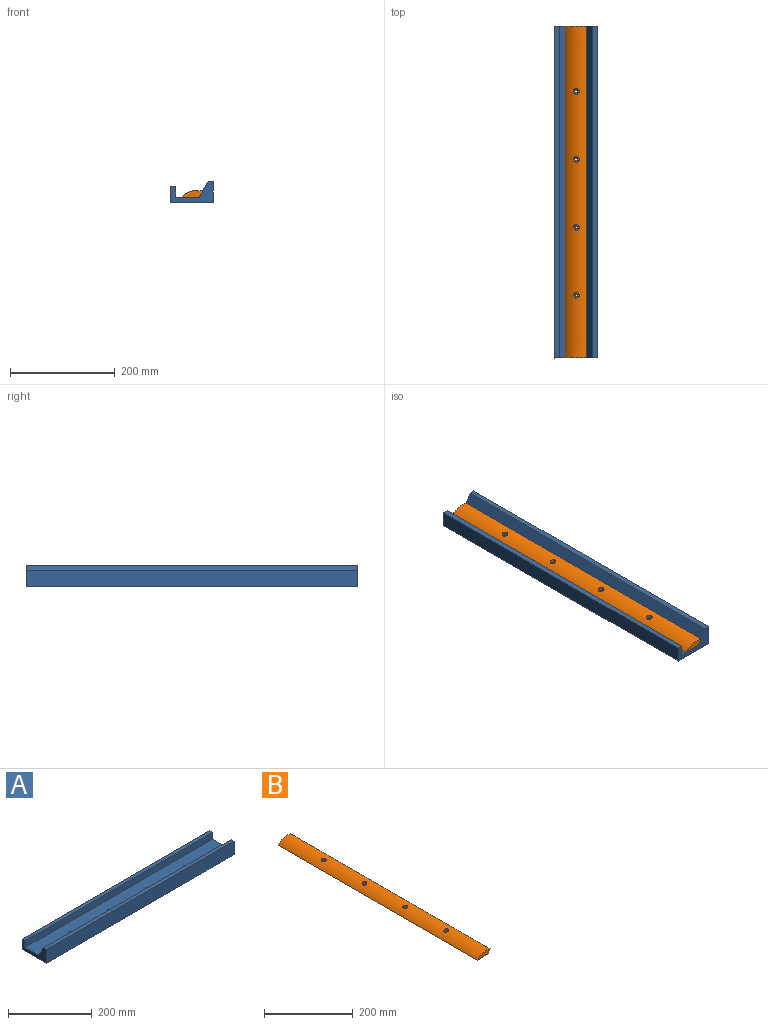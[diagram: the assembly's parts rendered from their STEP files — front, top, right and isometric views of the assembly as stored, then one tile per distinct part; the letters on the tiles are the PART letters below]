
ASSEMBLY  parts=2 mates=1
PART A: 14 faces, bbox 635x82x40 mm
  f0: plane 635x10mm, normal (0,0,1), area 6350mm2, adj f1,f2,f3,f9
  f1: plane 82x40mm, normal (-1,0,0), area 1579.8mm2, adj f0,f2,f4,f5,f6,f7,f8,f9
  f2: plane 635x40mm, normal (0,-1,0), area 25400mm2, adj f0,f1,f3,f5
  f3: plane 82x40mm, normal (1,0,0), area 1579.8mm2, adj f0,f2,f4,f5,f6,f7,f8,f9
  f4: plane 635x30mm, normal (0,1,0), area 19050mm2, adj f1,f3,f5,f6
  f5: plane 635x82mm, normal (0,0,-1), area 51975mm2, adj f1,f2,f3,f4,f10,f11,f12,f13
  f6: plane 635x10mm, normal (0,0,1), area 6350mm2, adj f1,f3,f4,f7
  f7: plane 635x20mm, normal (0,-1,0), area 12700mm2, adj f1,f3,f6,f8
  f8: plane 635x44.68mm, normal (0,0,1), area 28276.4mm2, adj f1,f3,f7,f9,f10,f11,f12,f13
  f9: plane 635x30mm, normal (0,0.87,0.5), area 21997mm2, adj f0,f1,f3,f8
  f10: cylinder r=2.75mm len=10mm, axis (0,0,1), area 172.8mm2, adj f5,f8
  f11: cylinder r=2.75mm len=10mm, axis (0,0,1), area 172.8mm2, adj f5,f8
  f12: cylinder r=2.75mm len=10mm, axis (0,0,1), area 172.8mm2, adj f5,f8
  f13: cylinder r=2.75mm len=10mm, axis (0,0,1), area 172.8mm2, adj f5,f8
PART B: 25 faces, bbox 40.8x635x13 mm
  f0: cylinder r=42mm len=635mm, axis (0,-1,0), area 27867.3mm2, adj f1,f2,f3,f4,f17,f19,f21,f23
  f1: plane 635x11.68mm, normal (0.87,0,-0.5), area 8567.7mm2, adj f0,f2,f3,f4
  f2: plane 635x34.06mm, normal (0,0,-1), area 21099.1mm2, adj f0,f1,f3,f4,f7,f10,f13,f16
  f3: plane 40.81x13mm, normal (0,1,0), area 364.3mm2, adj f0,f1,f2
  f4: plane 40.81x13mm, normal (0,-1,0), area 364.3mm2, adj f0,f1,f2
  f5: cylinder r=2.75mm len=5.5mm, axis (0,0,-1), area 69.1mm2, adj f6,f24
  f6: plane 13x13mm, normal (0,0,-1), area 109mm2, adj f5,f7
  f7: cylinder r=6.5mm len=13mm, axis (0,0,-1), area 102.1mm2, adj f2,f6
  f8: cylinder r=2.75mm len=5.5mm, axis (0,0,-1), area 69.1mm2, adj f9,f22
  f9: plane 13x13mm, normal (0,0,-1), area 109mm2, adj f8,f10
  f10: cylinder r=6.5mm len=13mm, axis (0,0,-1), area 102.1mm2, adj f2,f9
  f11: cylinder r=2.75mm len=5.5mm, axis (0,0,-1), area 69.1mm2, adj f12,f20
  f12: plane 13x13mm, normal (0,0,-1), area 109mm2, adj f11,f13
  f13: cylinder r=6.5mm len=13mm, axis (0,0,-1), area 102.1mm2, adj f2,f12
  f14: cylinder r=2.75mm len=5.5mm, axis (0,0,-1), area 69.1mm2, adj f15,f18
  f15: plane 13x13mm, normal (0,0,-1), area 109mm2, adj f14,f16
  f16: cylinder r=6.5mm len=13mm, axis (0,0,-1), area 102.1mm2, adj f2,f15
  f17: cylinder r=5.5mm len=11mm, axis (0,0,-1), area 180.4mm2, adj f0,f18
  f18: plane 11x11mm, normal (0,0,1), area 71.3mm2, adj f14,f17
  f19: cylinder r=5.5mm len=11mm, axis (0,0,-1), area 180.4mm2, adj f0,f20
  f20: plane 11x11mm, normal (0,0,1), area 71.3mm2, adj f11,f19
  f21: cylinder r=5.5mm len=11mm, axis (0,0,-1), area 180.4mm2, adj f0,f22
  f22: plane 11x11mm, normal (0,0,1), area 71.3mm2, adj f8,f21
  f23: cylinder r=5.5mm len=11mm, axis (0,0,-1), area 180.4mm2, adj f0,f24
  f24: plane 11x11mm, normal (0,0,1), area 71.3mm2, adj f5,f23
PLACE A rot(axis=(0,0,1),90deg) t=(102.95,333.47,235.65)mm
PLACE B t=(112.94,15.97,216.65)mm
MATE parallel A.f9 <-> B.f1  axis (-0.87,0,0.5) through (116.63,333.47,245.65)mm
